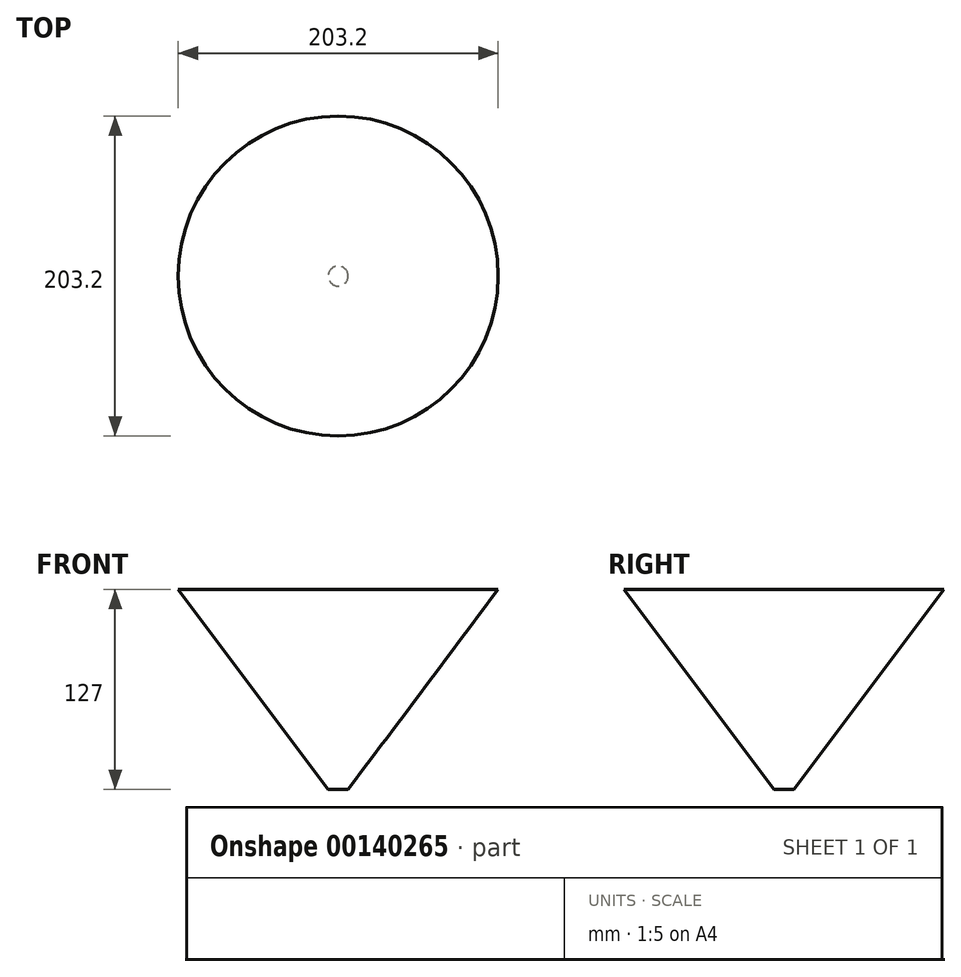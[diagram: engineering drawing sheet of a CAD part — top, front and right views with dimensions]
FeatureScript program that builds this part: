
annotation { "Feature Type Name" : "Feature", "Feature Type Description" : "" }
export const myFeature = defineFeature(function(context is Context, id is Id, definition is map)
    precondition{}
    {
        {
            var Q0;
            Q0=qCreatedBy(makeId("Front.planeOp"),FACE);
            var sketch = newSketch(context, id + "F0", { "sketchPlane" : qUnion([Q0])});
            skLineSegment(sketch, "E0", {"start": v(0, 127) * mm, "end": v(0, 0) * mm, "construction": true});
            skLineSegment(sketch, "E1", {"start": v(0, 127) * mm, "end": v(101.6, 127) * mm});
            skLineSegment(sketch, "E2", {"start": v(0, 0) * mm, "end": v(6.35, 0) * mm});
            skLineSegment(sketch, "E3", {"start": v(6.35, 0) * mm, "end": v(101.6, 127) * mm});
            skSolve(sketch);
        }
        {
            var Q0;
            Q0=sQuery(id+"F0.wireOp",EDGE,"E1");
            var Q1;
            Q1=sQuery(id+"F0.wireOp",EDGE,"E3");
            var Q2;
            Q2=sQuery(id+"F0.wireOp",EDGE,"E2");
            var Q3;
            Q3=sQuery(id+"F0.wireOp",EDGE,"E0");
            revolve(context, id + "F1", {"bodyType" : ToolBodyType.SURFACE, "operationType" : NewBodyOperationType.INTERSECT, "surfaceEntities" : qUnion([Q0, Q1, Q2]), "axis" : qUnion([Q3]), "revolveType" : RevolveType.FULL, "oppositeDirection" : true});
        }
    });
